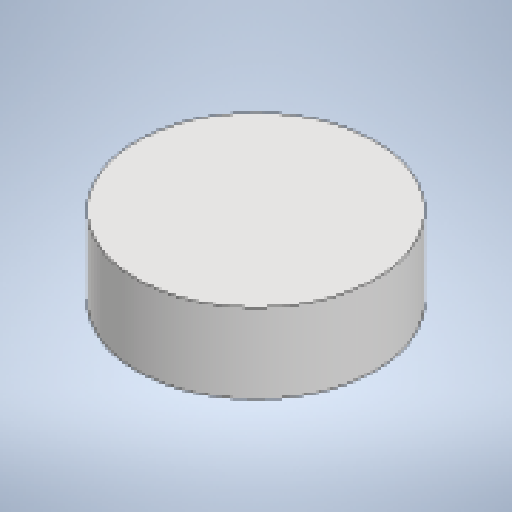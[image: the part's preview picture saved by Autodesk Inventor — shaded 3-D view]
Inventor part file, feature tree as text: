
AUTODESK INVENTOR PART (.ipt)
format: ipt  version: 2025.1 (Build 291241020, 241B)  size: 183,808 bytes
history: native  units: mm
features: sketch x8, extrude x1, revolve x1
ambient origin geometry x8: Origin, YZ Plane, XZ Plane, XY Plane, X Axis, Y Axis, Z Axis, Center Point
bodies: Solid1 (feature_tree)
feature tree (10):
  sketch  "Sketch1"  dims[d0=88.9mm d1=3.0mm]
  sketch  "Sketch2"  dims[d7=120.0mm d9=360.0deg]
  extrude  "Extrusion1"  Depth=3.0mm
  revolve  "Revolution1"  Angle=360.0deg
  sketch  "Sketch Circular Pattern1"  dims[d2=1200.0mm d3=120.0mm d5=360.0deg]
  sketch  "Sketch Circular Pattern2"  dims[d11=200.0mm]
  sketch  "Sketch Circular Pattern3"  dims[d12=120.0mm d14=360.0deg]
  sketch  "Sketch Circular Pattern4"  dims[d20=15.0deg]
  sketch  "Sketch3"  dims[d16=40.0mm d18=360.0deg]
  sketch  "Sketch4"  dims[d21=0.0mm d22=15.0deg d23=45.0deg d24=140.0mm d25=300.0mm d26=460.0mm d27=560.0mm d28=30.0mm d29=10.0mm d30=0.0mm d31=6.0mm d32=1803.421613mm d33=1200.0mm d37=100.0mm d38=30.0mm d39=1200.0mm d40=6.0mm d41=1200.0mm d42=253.289193mm d43=90.0deg]
